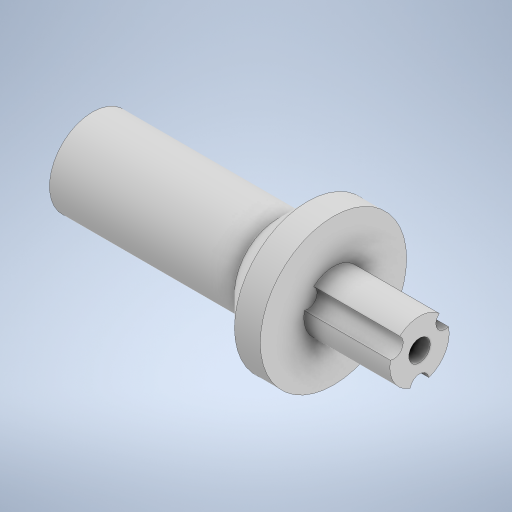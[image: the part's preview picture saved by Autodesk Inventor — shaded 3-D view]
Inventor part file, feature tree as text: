
AUTODESK INVENTOR PART (.ipt)
format: ipt  version: 2023 (Build 270158000, 158)  size: 286,720 bytes
history: native  units: mm
features: extrude x4, sketch x4, other x1, chamfer x1
ambient origin geometry x8: Origin, YZ Plane, XZ Plane, XY Plane, X Axis, Y Axis, Z Axis, Center Point
bodies: Body1 (feature_tree)
feature tree (10):
  other  "Твердое тело1"
  extrude  "Выдавливание1"  Depth=5.2mm
  extrude  "Выдавливание2"  Depth=1.9mm
  extrude  "Выдавливание3"  Depth=10.0mm
  chamfer  "Фаска1"  Distance=25.0mm
  extrude  "Выдавливание4"  Depth=6.9mm
  sketch  "Эскиз1"
  sketch  "Эскиз2"
  sketch  "Эскиз3"
  sketch  "Эскиз4"
